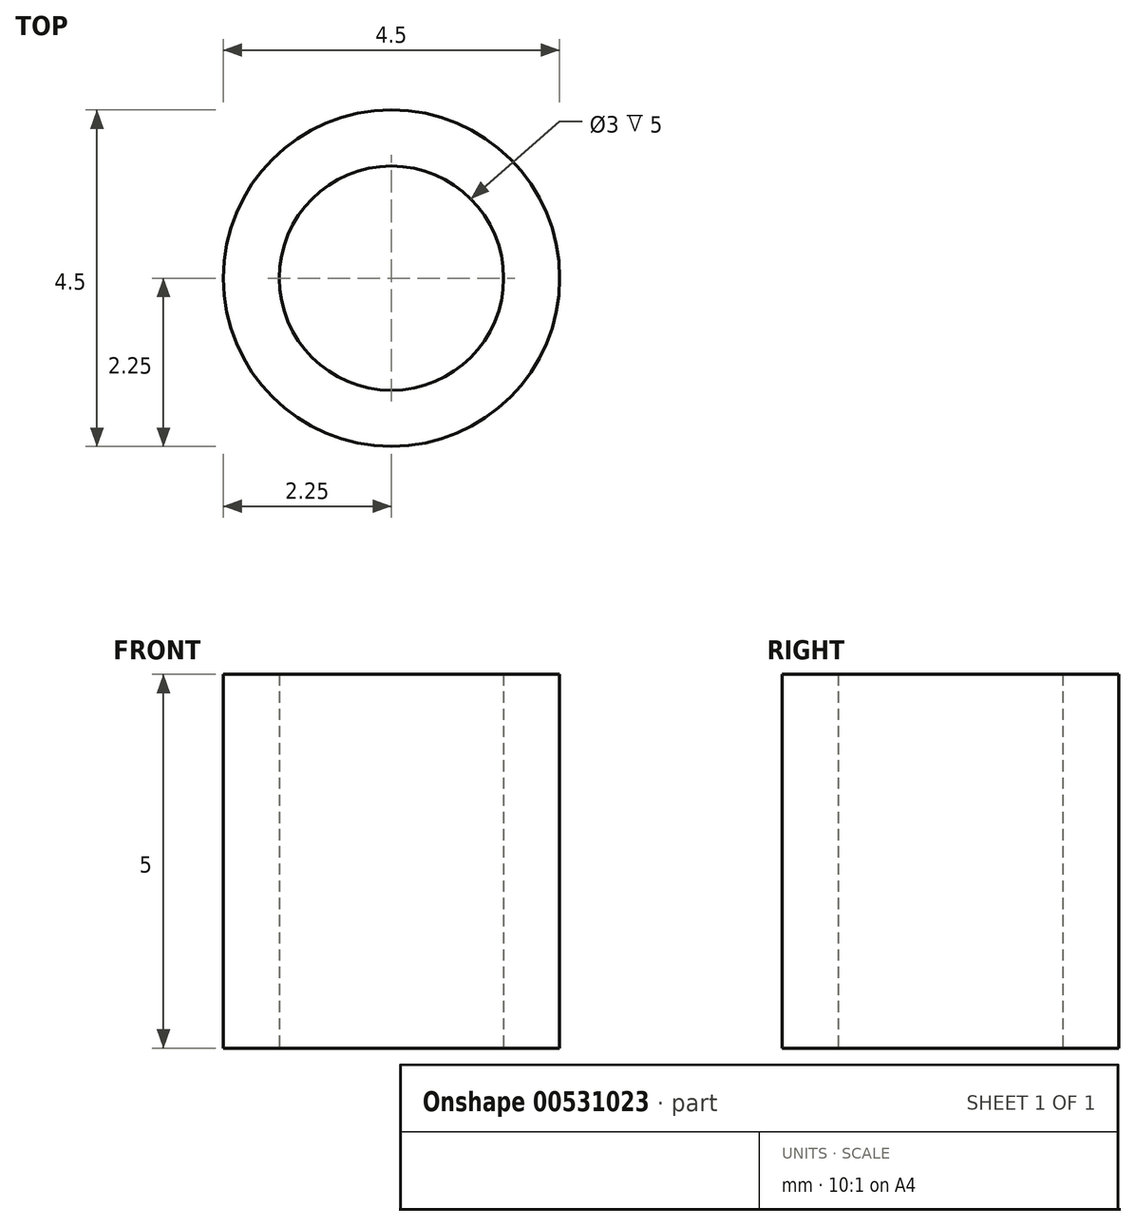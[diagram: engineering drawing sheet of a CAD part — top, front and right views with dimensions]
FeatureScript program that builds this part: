
annotation { "Feature Type Name" : "Feature", "Feature Type Description" : "" }
export const myFeature = defineFeature(function(context is Context, id is Id, definition is map)
    precondition{}
    {
        {
            var Q0;
            Q0=qCreatedBy(makeId("Top.planeOp"),FACE);
            var sketch = newSketch(context, id + "F0", { "sketchPlane" : qUnion([Q0])});
            skCircle(sketch, "E0", {"center": v(0, 0) * mm, "radius": 2.25 * mm});
            skCircle(sketch, "E1", {"center": v(0, 0) * mm, "radius": 1.5 * mm});
            skSolve(sketch);
        }
        {
            var Q0;
            Q0 = qSketchRegion(id + "F0", true);
            extrude(context, id + "F1", {"entities" : qUnion([Q0]), "depth" : 5 * mm, "offsetDistance" : 25 * mm});
        }
    });
